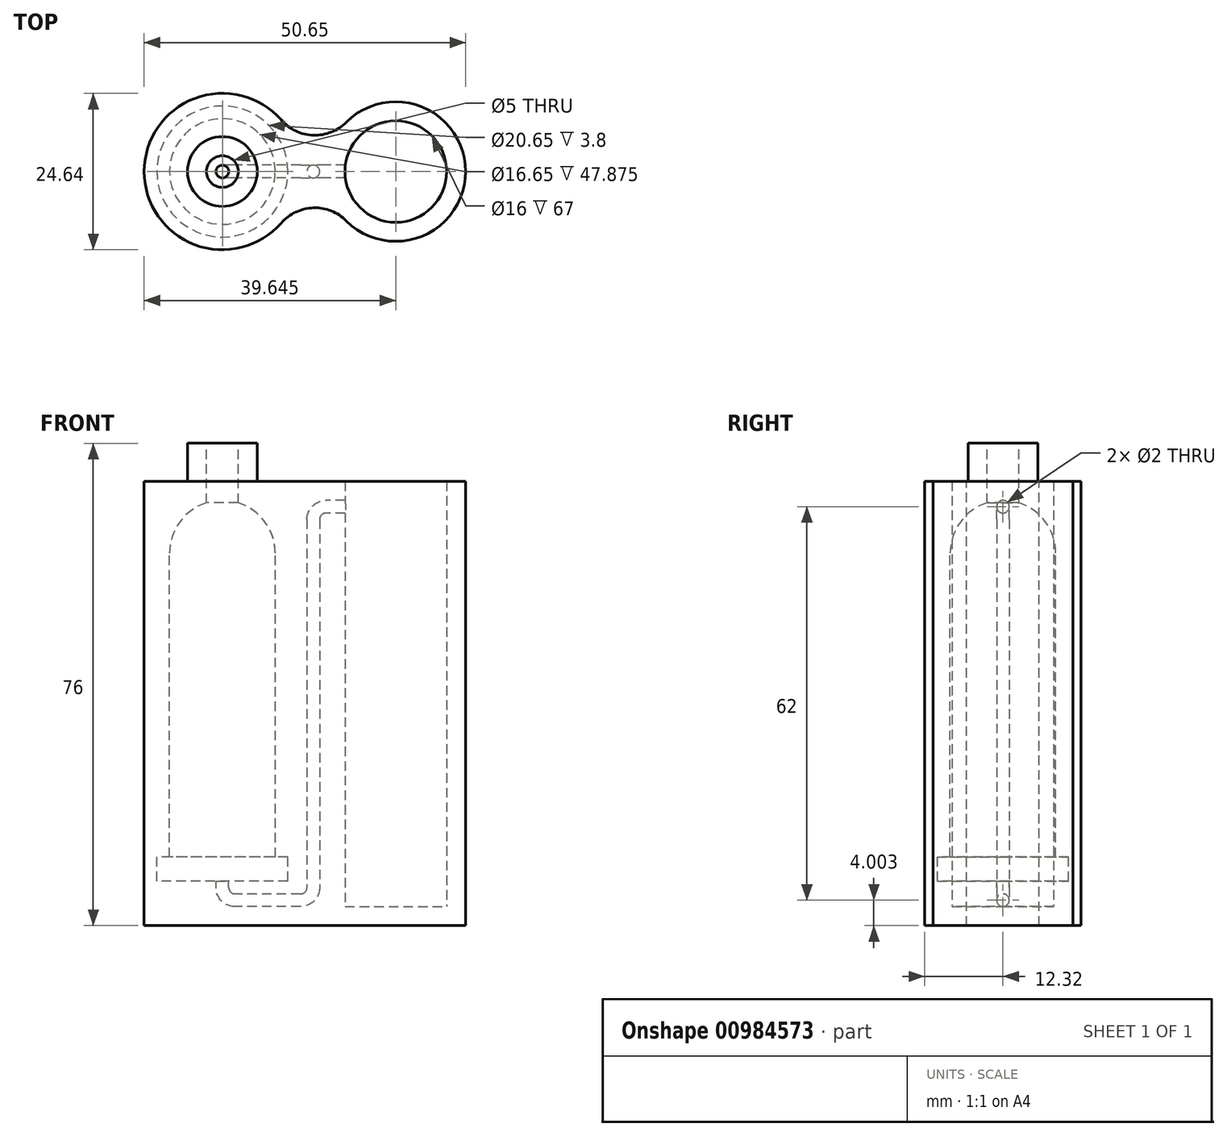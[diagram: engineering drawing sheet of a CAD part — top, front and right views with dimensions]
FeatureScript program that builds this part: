
annotation { "Feature Type Name" : "Feature", "Feature Type Description" : "" }
export const myFeature = defineFeature(function(context is Context, id is Id, definition is map)
    precondition{}
    {
        {
            var Q0;
            Q0=qCreatedBy(makeId("Front.planeOp"),FACE);
            var sketch = newSketch(context, id + "F0", { "sketchPlane" : qUnion([Q0])});
            skLineSegment(sketch, "E0.bottom", {"start": v(-8.32, 25.84) * mm, "end": v(8.32, 25.84) * mm});
            skLineSegment(sketch, "E0.top", {"start": v(-8.33, -25.84) * mm, "end": v(8.33, -25.84) * mm});
            skLineSegment(sketch, "E0.left", {"start": v(-8.32, 25.84) * mm, "end": v(-8.33, -25.84) * mm});
            skLineSegment(sketch, "E0.right", {"start": v(8.33, 25.84) * mm, "end": v(8.32, -25.84) * mm});
            skPoint(sketch, "E0.middle", {"position": v(0, 0) * mm});
            skCircle(sketch, "E1", {"center": v(0, 25.84) * mm, "radius": 8.33 * mm});
            skLineSegment(sketch, "E2.bottom", {"start": v(-12.32, 37.16) * mm, "end": v(12.32, 37.16) * mm});
            skLineSegment(sketch, "E2.top", {"start": v(-12.33, -32.84) * mm, "end": v(12.32, -32.84) * mm});
            skLineSegment(sketch, "E2.left", {"start": v(-12.32, 37.16) * mm, "end": v(-12.33, -32.84) * mm});
            skLineSegment(sketch, "E2.right", {"start": v(12.33, 37.16) * mm, "end": v(12.32, -32.84) * mm});
            skLineSegment(sketch, "E3", {"start": v(0, -25.84) * mm, "end": v(0, -32.84) * mm});
            skLineSegment(sketch, "E4", {"start": v(2, -28.84) * mm, "end": v(12.32, -28.84) * mm});
            skArc(sketch, "E5", {"start": v(2, -28.84) * mm, "mid": v(0.59, -28.25) * mm, "end": v(0, -26.84) * mm});
            skLineSegment(sketch, "E6", {"start": v(12.32, -27.84) * mm, "end": v(0, -27.84) * mm, "construction": true});
            skLineSegment(sketch, "E7", {"start": v(12.32, -29.84) * mm, "end": v(0, -29.84) * mm, "construction": true});
            skLineSegment(sketch, "E8", {"start": v(0, -26.84) * mm, "end": v(0, -25.84) * mm});
            skLineSegment(sketch, "E9", {"start": v(14.32, -26.84) * mm, "end": v(14.33, 31.16) * mm});
            skArc(sketch, "E10", {"start": v(12.32, -28.84) * mm, "mid": v(13.74, -28.25) * mm, "end": v(14.32, -26.84) * mm});
            skLineSegment(sketch, "E11.bottom", {"start": v(38.32, -32.84) * mm, "end": v(16.32, -32.84) * mm});
            skLineSegment(sketch, "E11.top", {"start": v(38.33, 37.16) * mm, "end": v(16.33, 37.16) * mm});
            skLineSegment(sketch, "E11.left", {"start": v(38.32, -32.84) * mm, "end": v(38.33, 37.16) * mm});
            skLineSegment(sketch, "E11.right", {"start": v(16.32, -32.84) * mm, "end": v(16.33, 37.16) * mm});
            skPoint(sketch, "E11.middle", {"position": v(27.32, 2.16) * mm});
            skLineSegment(sketch, "E12.bottom", {"start": v(19.33, 37.16) * mm, "end": v(35.33, 37.16) * mm});
            skLineSegment(sketch, "E12.top", {"start": v(19.32, -29.84) * mm, "end": v(35.32, -29.84) * mm});
            skLineSegment(sketch, "E12.left", {"start": v(19.33, 37.16) * mm, "end": v(19.32, -29.84) * mm});
            skLineSegment(sketch, "E12.right", {"start": v(35.33, 37.16) * mm, "end": v(35.32, -29.84) * mm});
            skLineSegment(sketch, "E13", {"start": v(27.32, -32.84) * mm, "end": v(27.32, -29.84) * mm});
            skArc(sketch, "E14", {"start": v(16.33, 33.16) * mm, "mid": v(14.91, 32.58) * mm, "end": v(14.33, 31.16) * mm});
            skLineSegment(sketch, "E15", {"start": v(16.33, 33.16) * mm, "end": v(21.9, 33.16) * mm});
            skLineSegment(sketch, "E16.bottom", {"start": v(-10.33, -22.04) * mm, "end": v(10.32, -22.04) * mm});
            skLineSegment(sketch, "E16.top", {"start": v(-10.33, -25.84) * mm, "end": v(10.32, -25.84) * mm});
            skLineSegment(sketch, "E16.left", {"start": v(-10.33, -22.04) * mm, "end": v(-10.33, -25.84) * mm});
            skLineSegment(sketch, "E16.right", {"start": v(10.32, -22.04) * mm, "end": v(10.32, -25.84) * mm});
            skLineSegment(sketch, "E17.bottom", {"start": v(-2.5, 37.16) * mm, "end": v(2.5, 37.16) * mm});
            skLineSegment(sketch, "E17.top", {"start": v(-2.5, 33.78) * mm, "end": v(2.5, 33.78) * mm});
            skLineSegment(sketch, "E17.left", {"start": v(-2.5, 37.16) * mm, "end": v(-2.5, 33.78) * mm});
            skLineSegment(sketch, "E17.right", {"start": v(2.5, 37.16) * mm, "end": v(2.5, 33.78) * mm});
            skLineSegment(sketch, "E18.bottom", {"start": v(2.5, 37.16) * mm, "end": v(-2.5, 37.16) * mm});
            skLineSegment(sketch, "E18.top", {"start": v(2.5, 43.16) * mm, "end": v(-2.5, 43.16) * mm});
            skLineSegment(sketch, "E18.left", {"start": v(2.5, 37.16) * mm, "end": v(2.5, 43.16) * mm});
            skLineSegment(sketch, "E18.right", {"start": v(-2.5, 37.16) * mm, "end": v(-2.5, 43.16) * mm});
            skPoint(sketch, "E18.middle", {"position": v(0, 40.16) * mm});
            skLineSegment(sketch, "E19", {"start": v(0, 43.16) * mm, "end": v(0, 34.16) * mm});
            skLineSegment(sketch, "E20.bottom", {"start": v(5.5, 43.16) * mm, "end": v(-5.5, 43.16) * mm});
            skLineSegment(sketch, "E20.top", {"start": v(5.5, 37.16) * mm, "end": v(-5.5, 37.16) * mm});
            skLineSegment(sketch, "E20.left", {"start": v(5.5, 43.16) * mm, "end": v(5.5, 37.16) * mm});
            skLineSegment(sketch, "E20.right", {"start": v(-5.5, 43.16) * mm, "end": v(-5.5, 37.16) * mm});
            skSolve(sketch);
        }
        {
            var Q0;
            {var subQ4=sQuery(id+"F0.wireOp",EDGE,"E2.left");Q0=makeQuery(id+"F0.imprint","IMPRINT",FACE,{"disambiguationData":[TD([[makeQuery(id+"F0.imprint","IMPRINT",EDGE,{"derivedFrom":subQ4}),1.0]])]});}
            var Q1;
            {var subQ0=sQuery(id+"F0.wireOp",EDGE,"E18.right");Q1=makeQuery(id+"F0.imprint","IMPRINT",FACE,{"disambiguationData":[TD([[makeQuery(id+"F0.imprint","IMPRINT",EDGE,{"derivedFrom":subQ0}),1.0]])]});}
            var Q2;
            Q2=sQuery(id+"F0.wireOp",EDGE,"E3");
            revolve(context, id + "F1", {"surfaceOperationType" : NewSurfaceOperationType.NEW, "entities" : qUnion([Q0, Q1]), "axis" : qUnion([Q2]), "revolveType" : RevolveType.FULL});
        }
        {
            var Q0;
            Q0=qCreatedBy(makeId("Right.planeOp"),FACE);
            var Q1;
            Q1=sQuery(id+"F0.wireOp",VERTEX,"E4.end");
            cPlane(context, id + "F2", {"entities" : qUnion([Q0, Q1]), "cplaneType" : CPlaneType.PLANE_POINT, "offset" : 25 * mm, "width" : 150 * mm, "height" : 150 * mm});
        }
        {
            var Q0;
            Q0=qCreatedBy(id+"F2.planeOp",FACE);
            var sketch = newSketch(context, id + "F3", { "sketchPlane" : qUnion([Q0])});
            skCircle(sketch, "E21", {"center": v(0, -28.84) * mm, "radius": 1 * mm});
            skSolve(sketch);
        }
        {
            var Q0;
            {var subQ3=sQuery(id+"F0.wireOp",EDGE,"E11.right");Q0=makeQuery(id+"F0.imprint","IMPRINT",FACE,{"disambiguationData":[TD([[makeQuery(id+"F0.imprint","IMPRINT",EDGE,{"derivedFrom":subQ3}),-1.0]])]});}
            var Q1;
            {var subQ3=sQuery(id+"F0.wireOp",EDGE,"E13");Q1=makeQuery(id+"F0.imprint","IMPRINT",FACE,{"disambiguationData":[TD([[makeQuery(id+"F0.imprint","IMPRINT",EDGE,{"derivedFrom":subQ3}),1.0]])]});}
            var Q2;
            Q2=sQuery(id+"F0.wireOp",EDGE,"E13");
            revolve(context, id + "F4", {"surfaceOperationType" : NewSurfaceOperationType.NEW, "entities" : qUnion([Q0, Q1]), "axis" : qUnion([Q2]), "revolveType" : RevolveType.FULL});
        }
        {
            var Q0;
            Q0=qCreatedBy(makeId("Right.planeOp"),FACE);
            var Q1;
            Q1=sQuery(id+"F0.wireOp",VERTEX,"E11.bottom.end");
            cPlane(context, id + "F5", {"entities" : qUnion([Q0, Q1]), "cplaneType" : CPlaneType.PLANE_POINT, "offset" : 25 * mm, "width" : 150 * mm, "height" : 150 * mm});
        }
        {
            var Q0;
            Q0=makeQuery(id+"F1.opRevolve","SWEPT_FACE",FACE,{"disambiguationData":[OSD([sQuery(id+"F0.wireOp",EDGE,"E2.bottom")])]});
            var sketch = newSketch(context, id + "F6", { "sketchPlane" : qUnion([Q0])});
            skCircle(sketch, "E22", {"center": v(0, 0) * mm, "radius": 12.32 * mm});
            skCircle(sketch, "E23", {"center": v(27.32, 0) * mm, "radius": 11 * mm});
            skLineSegment(sketch, "E24", {"start": v(27.32, 0) * mm, "end": v(19.55, 7.78) * mm, "construction": true});
            skArc(sketch, "E25", {"start": v(9.27, 8.12) * mm, "mid": v(14.34, 5.72) * mm, "end": v(19.55, 7.78) * mm});
            skArc(sketch, "E26.MirrorCS", {"start": v(9.27, -8.12) * mm, "mid": v(14.34, -5.72) * mm, "end": v(19.55, -7.78) * mm});
            skSolve(sketch);
        }
        {
            var Q0;
            {var subQ0=sQuery(id+"F6.wireOp",EDGE,"E25");Q0=makeQuery(id+"F6.imprint","IMPRINT",FACE,{"disambiguationData":[TD([[makeQuery(id+"F6.imprint","IMPRINT",EDGE,{"derivedFrom":subQ0}),-1.0]])]});}
            extrude(context, id + "F7", {"entities" : qUnion([Q0]), "operationType" : NewBodyOperationType.ADD, "oppositeDirection" : true, "depth" : 70 * mm, "offsetDistance" : 25 * mm});
        }
        {
            var Q0;
            Q0=makeQuery(id+"F3.imprint","IMPRINT",FACE,{"disambiguationData":[TD([[makeQuery(id+"F3.imprint","IMPRINT",EDGE,{"derivedFrom":sQuery(id+"F3.wireOp",EDGE,"E21")}),1.0]])]});
            var Q1;
            Q1=sQuery(id+"F0.wireOp",EDGE,"E8");
            var Q2;
            Q2=sQuery(id+"F0.wireOp",EDGE,"E5");
            var Q3;
            Q3=sQuery(id+"F0.wireOp",EDGE,"E4");
            var Q4;
            Q4=sQuery(id+"F0.wireOp",EDGE,"E10");
            var Q5;
            Q5=sQuery(id+"F0.wireOp",EDGE,"E9");
            var Q6;
            Q6=sQuery(id+"F0.wireOp",EDGE,"E14");
            var Q7;
            Q7=sQuery(id+"F0.wireOp",EDGE,"E15");
            sweep(context, id + "F8", {"operationType" : NewBodyOperationType.REMOVE, "profiles" : qUnion([Q0]), "path" : qUnion([Q1, Q2, Q3, Q4, Q5, Q6, Q7])});
        }
    });
